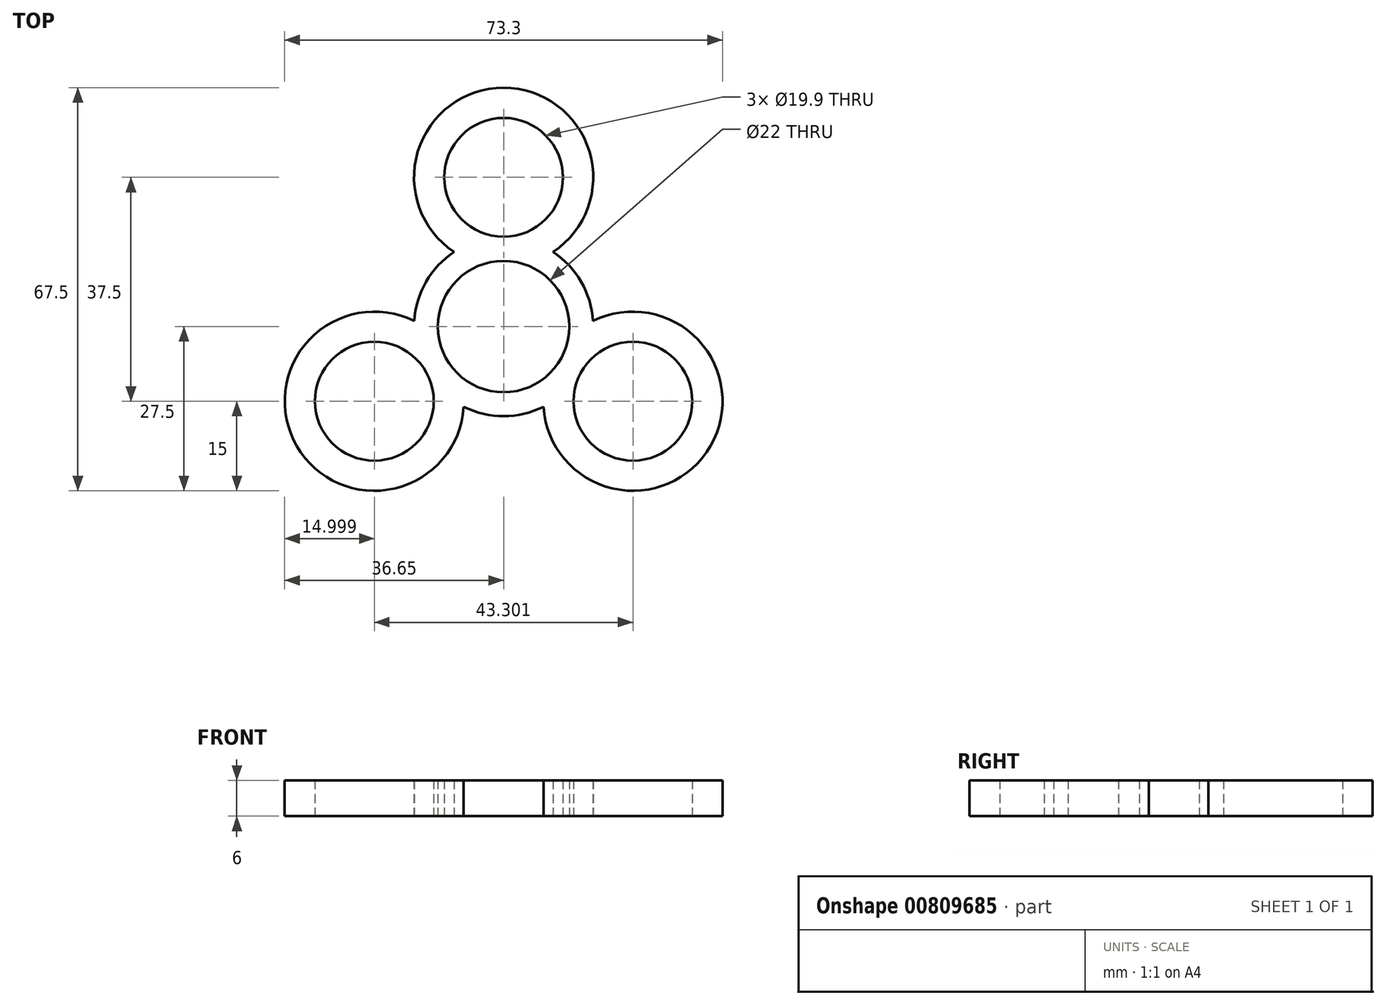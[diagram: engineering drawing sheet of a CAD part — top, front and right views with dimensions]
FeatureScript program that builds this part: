
annotation { "Feature Type Name" : "Feature", "Feature Type Description" : "" }
export const myFeature = defineFeature(function(context is Context, id is Id, definition is map)
    precondition{}
    {
        {
            var Q0;
            Q0=qCreatedBy(makeId("Top.planeOp"),FACE);
            var sketch = newSketch(context, id + "F0", { "sketchPlane" : qUnion([Q0])});
            skArc(sketch, "E0", {"start": v(9.53, 5.5) * mm, "mid": v(0, 11) * mm, "end": v(-9.53, 5.5) * mm});
            skLineSegment(sketch, "E1", {"start": v(0, 0) * mm, "end": v(0, 25) * mm});
            skCircle(sketch, "E2", {"center": v(0, 25) * mm, "radius": 9.95 * mm});
            skArc(sketch, "E3", {"start": v(-8.3, 12.5) * mm, "mid": v(-10.93, 10.27) * mm, "end": v(-13, 7.5) * mm});
            skArc(sketch, "E4", {"start": v(8.3, 12.5) * mm, "mid": v(0, 40) * mm, "end": v(-8.3, 12.5) * mm});
            skArc(sketch, "E5.trimOffspring", {"start": v(13, 7.5) * mm, "mid": v(10.93, 10.27) * mm, "end": v(8.3, 12.5) * mm});
            skPoint(sketch, "E6.orphan", {"position": v(36.65, 21.16) * mm});
            skPoint(sketch, "E7.orphan", {"position": v(-36.65, 21.16) * mm});
            skArc(sketch, "E8.1.0", {"start": v(-14.97, 0.93) * mm, "mid": v(-34.64, -20) * mm, "end": v(-6.68, -13.43) * mm});
            skArc(sketch, "E8.1.1", {"start": v(-6.68, -13.43) * mm, "mid": v(-3.43, -14.6) * mm, "end": v(0, -15) * mm});
            skArc(sketch, "E8.1.2", {"start": v(-13, 7.5) * mm, "mid": v(-14.36, 4.33) * mm, "end": v(-14.97, 0.93) * mm});
            skCircle(sketch, "E8.1.3", {"center": v(-21.65, -12.5) * mm, "radius": 9.95 * mm});
            skArc(sketch, "E8.1.4", {"start": v(-9.53, 5.5) * mm, "mid": v(-9.53, -5.5) * mm, "end": v(0, -11) * mm});
            skArc(sketch, "E8.2.0", {"start": v(6.68, -13.43) * mm, "mid": v(34.64, -20) * mm, "end": v(14.97, 0.93) * mm});
            skArc(sketch, "E8.2.1", {"start": v(14.97, 0.93) * mm, "mid": v(14.36, 4.33) * mm, "end": v(13, 7.5) * mm});
            skArc(sketch, "E8.2.2", {"start": v(0, -15) * mm, "mid": v(3.43, -14.6) * mm, "end": v(6.68, -13.43) * mm});
            skCircle(sketch, "E8.2.3", {"center": v(21.65, -12.5) * mm, "radius": 9.95 * mm});
            skArc(sketch, "E8.2.4", {"start": v(0, -11) * mm, "mid": v(9.53, -5.5) * mm, "end": v(9.53, 5.5) * mm});
            skSolve(sketch);
        }
        {
            var Q0;
            Q0=makeQuery(id+"F0.imprint","IMPRINT",FACE,{"disambiguationData":[TD([[makeQuery(id+"F0.imprint","IMPRINT",EDGE,{"derivedFrom":sQuery(id+"F0.wireOp",EDGE,"E2")}),-1.0]])]});
            extrude(context, id + "F1", {"entities" : qUnion([Q0]), "depth" : 6 * mm, "offsetDistance" : 25 * mm});
        }
    });
